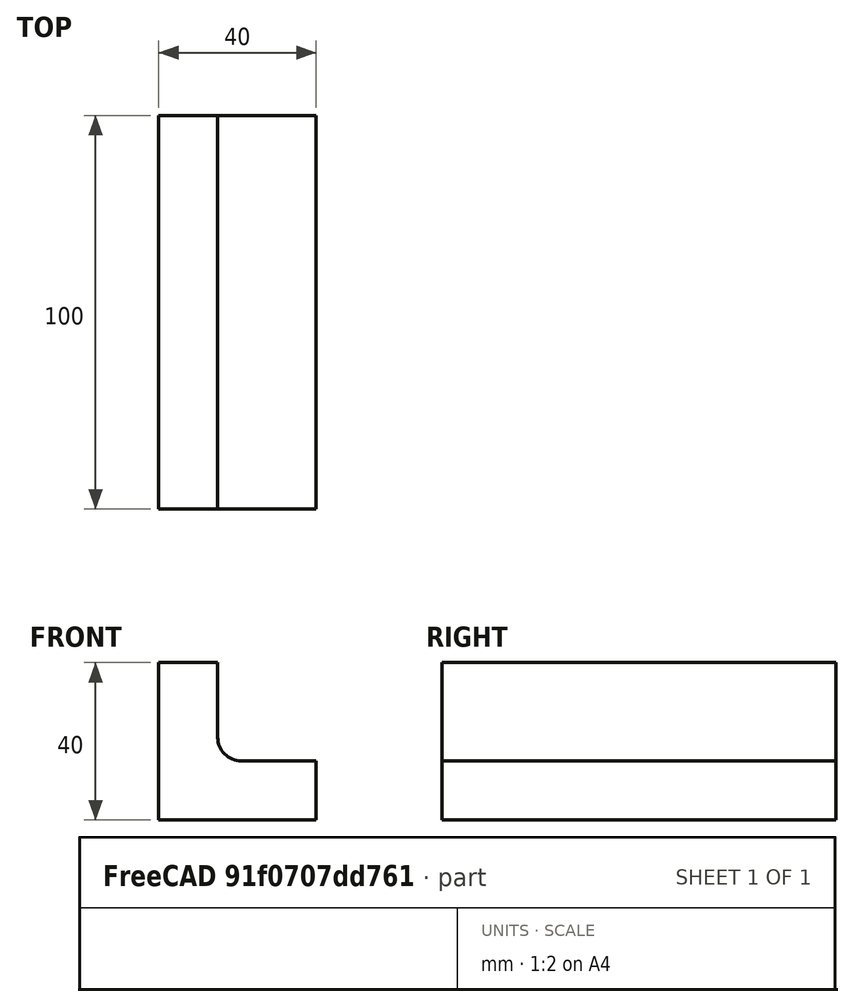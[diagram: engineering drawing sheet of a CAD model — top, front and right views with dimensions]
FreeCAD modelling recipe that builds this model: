
FCSTD DOCUMENT  (FreeCAD 0.16R6707 (Git))
Label: Refuerzo_L
License: CreativeCommons Attribution-ShareAlike
LicenseURL: http://creativecommons.org/licenses/by-sa/4.0/
objects: Sketcher::SketchObject×1, PartDesign::Pad×1
note: 3 computed .brp shape members not serialized (recipe doc carries the construction recipe); baked Part::Feature solids carry a one-line shape summary decoded from their .brp

FEATURE [Sketcher::SketchObject] Sketch  label="Boceto_L"
  Placement = pos=(0,0,0) rot=(-1,0,0;4.71239rad)
  sketch-geometry (7):
    g0: LineSegment StartX=0 StartY=0 StartZ=0 EndX=0 EndY=40 EndZ=0
    g1: LineSegment StartX=0 StartY=40 StartZ=0 EndX=15 EndY=40 EndZ=0
    g2: LineSegment StartX=15 StartY=40 StartZ=0 EndX=15 EndY=21 EndZ=0
    g3: LineSegment StartX=21 StartY=15 StartZ=0 EndX=40 EndY=15 EndZ=0
    g4: LineSegment StartX=40 StartY=15 StartZ=0 EndX=40 EndY=0 EndZ=0
    g5: LineSegment StartX=40 StartY=0 StartZ=0 EndX=0 EndY=0 EndZ=0
    g6: ArcOfCircle CenterX=21 CenterY=21 CenterZ=0 NormalX=0 NormalY=0 NormalZ=1 Radius=6 StartAngle=3.14159 EndAngle=4.71239
  constraints (19):
    c: Coincident(g-1,g0)
    c: Vertical(g0)
    c: Coincident(g0,g1)
    c: Coincident(g1,g2)
    c: Vertical(g2)
    c: Horizontal(g3)
    c: Coincident(g3,g4)
    c: Coincident(g4,g5)
    c: Coincident(g0,g5)
    c: Parallel(g5,g3)
    c: Parallel(g1,g5)
    c: Equal(g1,g4)
    c: Parallel(g4,g0)
    c: DistanceY(g0,g0) = 40
    c: DistanceX(g1,g1) = 15
    c: Equal(g5,g0)
    c: Tangent(g2,g6) = -1.5708
    c: Tangent(g3,g6) = -1.5708
    c: Radius(g6) = 6
FEATURE [PartDesign::Pad] Pad  label="Refuerzo_L"
  Length = 100
  Length2 = 100
  Placement = pos=(0,0,0) rot=(-1,0,0;4.71239rad)
  Sketch = -> Sketch
  Type = 0
